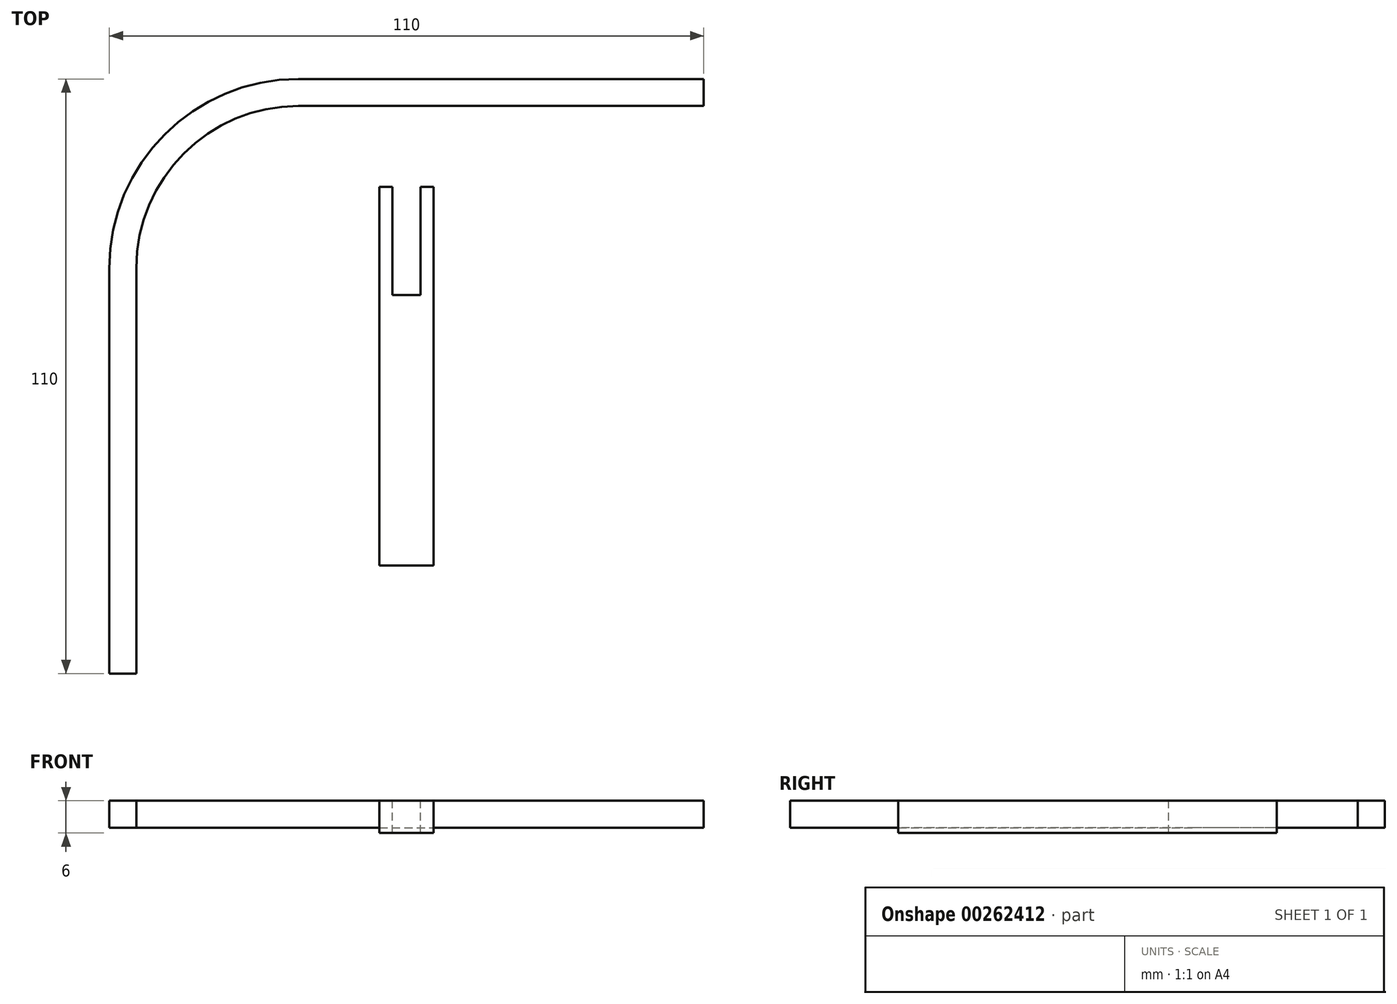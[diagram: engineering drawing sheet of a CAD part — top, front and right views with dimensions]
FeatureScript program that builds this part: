
annotation { "Feature Type Name" : "Feature", "Feature Type Description" : "" }
export const myFeature = defineFeature(function(context is Context, id is Id, definition is map)
    precondition{}
    {
        {
            var Q0;
            Q0=qCreatedBy(makeId("Top.planeOp"),FACE);
            var sketch = newSketch(context, id + "F0", { "sketchPlane" : qUnion([Q0])});
            skLineSegment(sketch, "E0.bottom", {"start": v(55, -55) * mm, "end": v(-55, -55) * mm, "construction": true});
            skLineSegment(sketch, "E0.top", {"start": v(55, 55) * mm, "end": v(-55, 55) * mm, "construction": true});
            skLineSegment(sketch, "E0.left", {"start": v(55, -55) * mm, "end": v(55, 55) * mm, "construction": true});
            skLineSegment(sketch, "E0.right", {"start": v(-55, -55) * mm, "end": v(-55, 55) * mm, "construction": true});
            skPoint(sketch, "E0.middle", {"position": v(0, 0) * mm});
            skLineSegment(sketch, "E1", {"start": v(55, 55) * mm, "end": v(-20, 55) * mm});
            skLineSegment(sketch, "E2", {"start": v(-55, 20) * mm, "end": v(-55, -55) * mm});
            skLineSegment(sketch, "E3", {"start": v(-55, -55) * mm, "end": v(-50, -55) * mm});
            skLineSegment(sketch, "E4", {"start": v(-50, -55) * mm, "end": v(-50, 20) * mm});
            skLineSegment(sketch, "E5", {"start": v(-20, 50) * mm, "end": v(55, 50) * mm});
            skLineSegment(sketch, "E6", {"start": v(55, 50) * mm, "end": v(55, 55) * mm});
            skPoint(sketch, "E7.visualSharp", {"position": v(-50, 50) * mm});
            skArc(sketch, "E7.filletArc", {"start": v(-20, 50) * mm, "mid": v(-41.21, 41.21) * mm, "end": v(-50, 20) * mm});
            skPoint(sketch, "E8.visualSharp", {"position": v(-55, 55) * mm});
            skArc(sketch, "E8.filletArc", {"start": v(-20, 55) * mm, "mid": v(-44.75, 44.75) * mm, "end": v(-55, 20) * mm});
            skLineSegment(sketch, "E9.bottom", {"start": v(5, -35) * mm, "end": v(-5, -35) * mm});
            skLineSegment(sketch, "E9.top", {"start": v(5, 35) * mm, "end": v(-5, 35) * mm});
            skLineSegment(sketch, "E9.left", {"start": v(5, -35) * mm, "end": v(5, 35) * mm});
            skLineSegment(sketch, "E9.right", {"start": v(-5, -35) * mm, "end": v(-5, 35) * mm});
            skPoint(sketch, "E10", {"position": v(0, 35) * mm});
            skLineSegment(sketch, "E11.bottom", {"start": v(-2.6, 35) * mm, "end": v(2.6, 35) * mm});
            skLineSegment(sketch, "E11.top", {"start": v(-2.6, 15) * mm, "end": v(2.6, 15) * mm});
            skLineSegment(sketch, "E11.left", {"start": v(-2.6, 35) * mm, "end": v(-2.6, 15) * mm});
            skLineSegment(sketch, "E11.right", {"start": v(2.6, 35) * mm, "end": v(2.6, 15) * mm});
            skSolve(sketch);
        }
        {
            var Q0;
            Q0=makeQuery(id+"F0.imprint","IMPRINT",FACE,{"disambiguationData":[TD([[makeQuery(id+"F0.imprint","IMPRINT",EDGE,{"derivedFrom":sQuery(id+"F0.wireOp",EDGE,"E1")}),1.0]])]});
            extrude(context, id + "F1", {"entities" : qUnion([Q0]), "depth" : 5 * mm});
        }
        {
            var Q0;
            Q0=makeQuery(id+"F0.imprint","IMPRINT",FACE,{"disambiguationData":[TD([[makeQuery(id+"F0.imprint","IMPRINT",EDGE,{"derivedFrom":sQuery(id+"F0.wireOp",EDGE,"E9.bottom")}),-1.0]])]});
            var Q1;
            Q1=makeQuery(id+"F0.imprint","IMPRINT",FACE,{"disambiguationData":[TD([[makeQuery(id+"F0.imprint","IMPRINT",EDGE,{"derivedFrom":sQuery(id+"F0.wireOp",EDGE,"E11.bottom")}),-1.0]])]});
            extrude(context, id + "F2", {"entities" : qUnion([Q0, Q1]), "oppositeDirection" : true, "depth" : 1 * mm});
        }
        {
            var Q0;
            Q0=makeQuery(id+"F0.imprint","IMPRINT",FACE,{"disambiguationData":[TD([[makeQuery(id+"F0.imprint","IMPRINT",EDGE,{"derivedFrom":sQuery(id+"F0.wireOp",EDGE,"E9.bottom")}),-1.0]])]});
            extrude(context, id + "F3", {"entities" : qUnion([Q0]), "operationType" : NewBodyOperationType.ADD, "depth" : 5 * mm});
        }
    });
